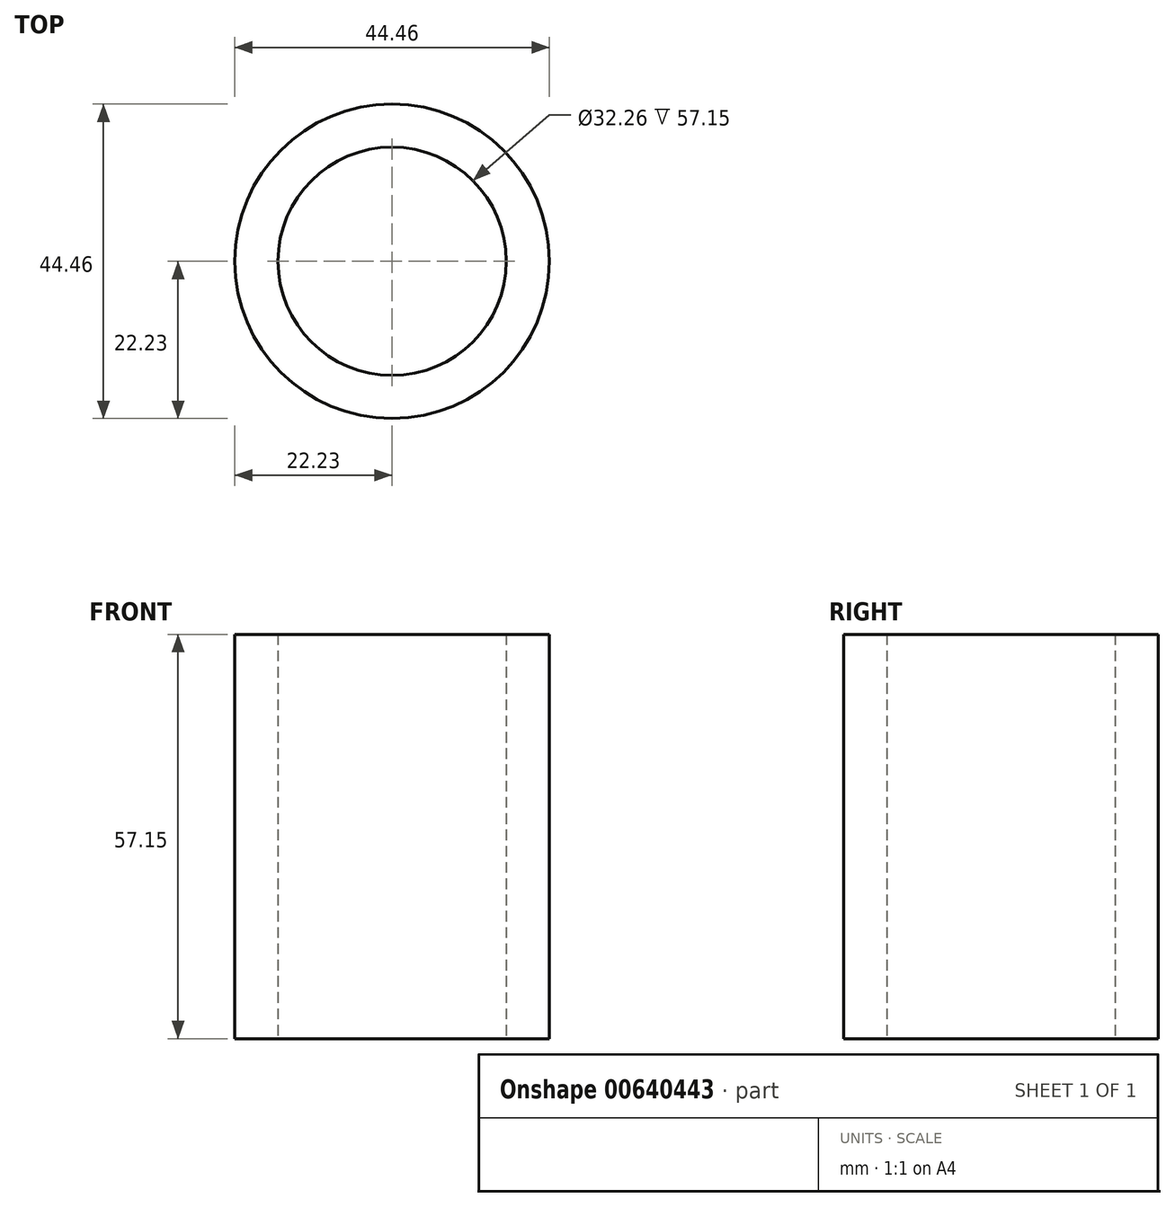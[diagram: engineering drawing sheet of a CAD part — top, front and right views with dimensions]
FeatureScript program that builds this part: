
annotation { "Feature Type Name" : "Feature", "Feature Type Description" : "" }
export const myFeature = defineFeature(function(context is Context, id is Id, definition is map)
    precondition{}
    {
        {
            var Q0;
            Q0=qCreatedBy(makeId("Top.planeOp"),FACE);
            var sketch = newSketch(context, id + "F0", { "sketchPlane" : qUnion([Q0])});
            skCircle(sketch, "E0", {"center": v(0, 0) * mm, "radius": 16.13 * mm});
            skCircle(sketch, "E1", {"center": v(0, 0) * mm, "radius": 22.23 * mm});
            skSolve(sketch);
        }
        {
            var Q0;
            Q0 = qSketchRegion(id + "F0", true);
            extrude(context, id + "F1", {"entities" : qUnion([Q0]), "depth" : 57.15 * mm, "offsetDistance" : 25.4 * mm});
        }
    });
